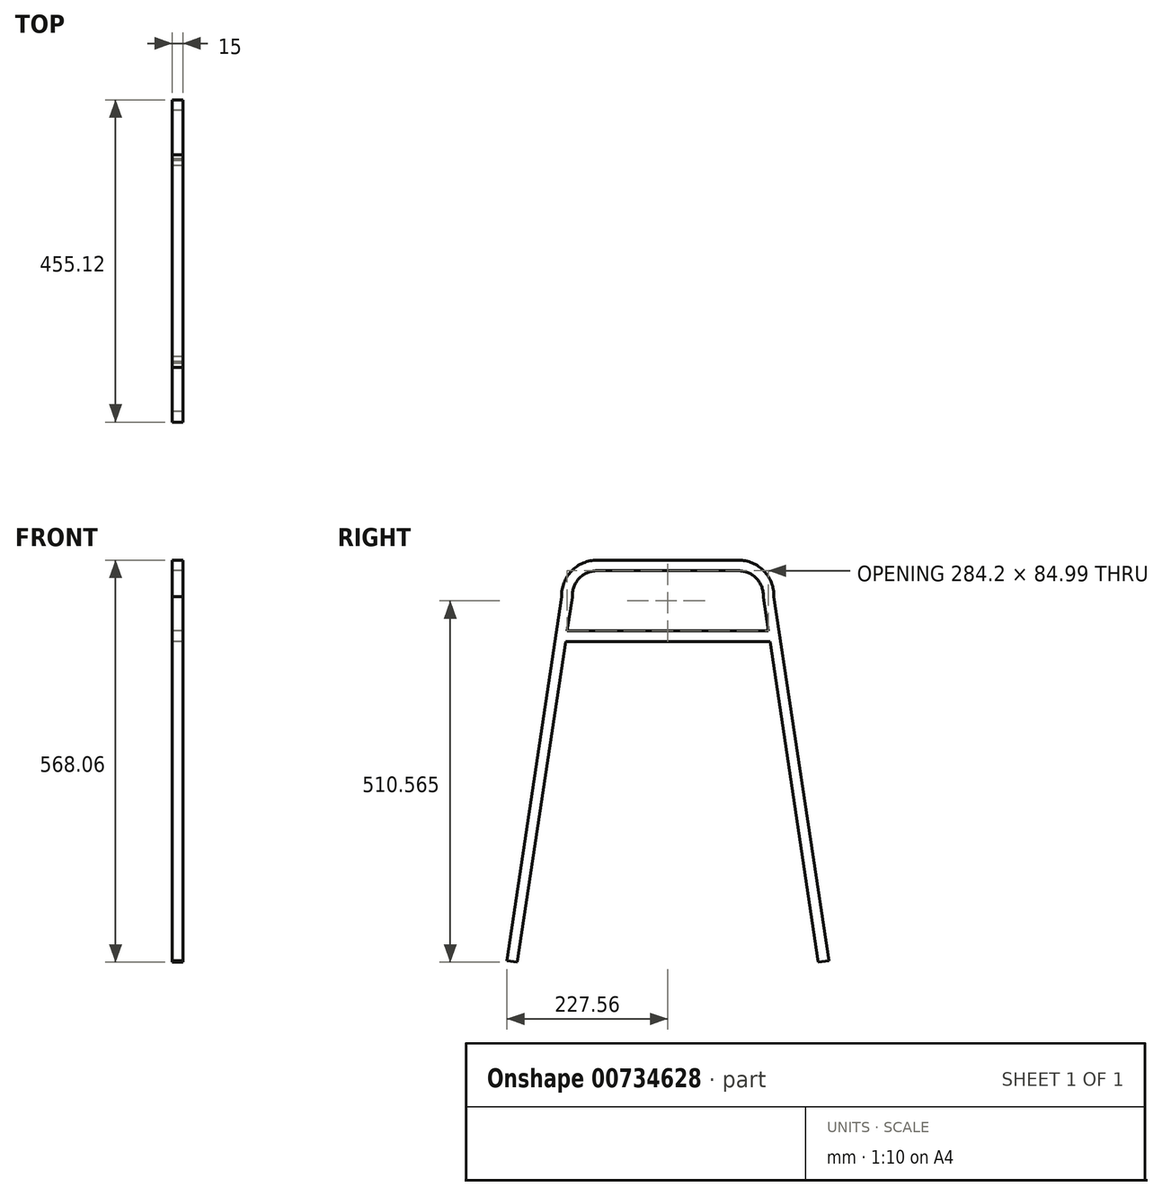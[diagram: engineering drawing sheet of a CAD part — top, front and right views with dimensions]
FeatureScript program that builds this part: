
annotation { "Feature Type Name" : "Feature", "Feature Type Description" : "" }
export const myFeature = defineFeature(function(context is Context, id is Id, definition is map)
    precondition{}
    {
        {
            var Q0;
            Q0=qCreatedBy(makeId("Right.planeOp"),FACE);
            var sketch = newSketch(context, id + "F0", { "sketchPlane" : qUnion([Q0])});
            skLineSegment(sketch, "E0", {"start": v(-149.97, 31.24) * mm, "end": v(-227.56, -482.94) * mm});
            skLineSegment(sketch, "E1", {"start": v(0, 82.88) * mm, "end": v(-100, 82.88) * mm});
            skArc(sketch, "E2", {"start": v(-100, 82.88) * mm, "mid": v(-135.93, 67.65) * mm, "end": v(-149.97, 31.24) * mm});
            skLineSegment(sketch, "E3", {"start": v(0, 82.88) * mm, "end": v(0, -474.43) * mm, "construction": true});
            skLineSegment(sketch, "E4.MirrorCS", {"start": v(149.97, 31.24) * mm, "end": v(227.56, -482.94) * mm});
            skLineSegment(sketch, "E5.MirrorCS", {"start": v(0, 82.88) * mm, "end": v(100, 82.88) * mm});
            skArc(sketch, "E6.MirrorCS", {"start": v(100, 82.88) * mm, "mid": v(135.93, 67.65) * mm, "end": v(149.97, 31.24) * mm});
            skLineSegment(sketch, "E7.0", {"start": v(-134.92, 30.48) * mm, "end": v(-142.1, -17.11) * mm});
            skArc(sketch, "E7.1", {"start": v(-100, 67.88) * mm, "mid": v(-125.58, 56.77) * mm, "end": v(-134.92, 30.48) * mm});
            skLineSegment(sketch, "E7.2", {"start": v(134.92, 30.48) * mm, "end": v(142.1, -17.11) * mm});
            skArc(sketch, "E7.3", {"start": v(100, 67.88) * mm, "mid": v(125.58, 56.77) * mm, "end": v(134.92, 30.48) * mm});
            skLineSegment(sketch, "E7.4", {"start": v(0, 67.88) * mm, "end": v(100, 67.88) * mm});
            skLineSegment(sketch, "E7.5", {"start": v(0, 67.88) * mm, "end": v(-100, 67.88) * mm});
            skLineSegment(sketch, "E8", {"start": v(-144.36, -32.11) * mm, "end": v(144.36, -32.11) * mm});
            skLineSegment(sketch, "E9.0", {"start": v(-142.1, -17.11) * mm, "end": v(142.1, -17.11) * mm});
            skLineSegment(sketch, "E10.trimOffspring", {"start": v(-144.36, -32.11) * mm, "end": v(-212.72, -485.18) * mm});
            skLineSegment(sketch, "E11.trimOffspring", {"start": v(144.36, -32.11) * mm, "end": v(212.72, -485.18) * mm});
            skLineSegment(sketch, "E12", {"start": v(-212.72, -485.18) * mm, "end": v(-227.56, -482.94) * mm});
            skLineSegment(sketch, "E13", {"start": v(212.72, -485.18) * mm, "end": v(227.56, -482.94) * mm});
            skSolve(sketch);
        }
        {
            var Q0;
            Q0 = qSketchRegion(id + "F0", true);
            extrude(context, id + "F1", {"entities" : qUnion([Q0]), "depth" : 15 * mm, "offsetDistance" : 25 * mm});
        }
    });
